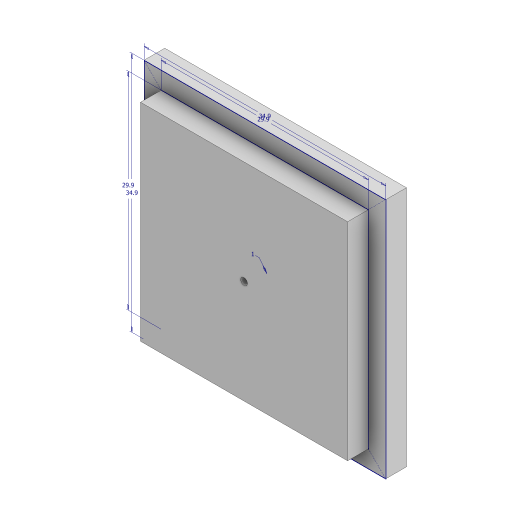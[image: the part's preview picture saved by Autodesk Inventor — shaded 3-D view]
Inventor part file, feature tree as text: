
AUTODESK INVENTOR PART (.ipt)
format: ipt  version: 2023 (Build 270158000, 158)  size: 114,688 bytes
history: native  units: in
note: dims shown in document units (in); Inventor stores cm internally (conversion verified against a paired STEP export)
features: extrude x2, sketch x1
ambient origin geometry x8: Origin, YZ Plane, XZ Plane, XY Plane, X Axis, Y Axis, Z Axis, Center Point
bodies: Solid1 (feature_tree)
feature tree (3):
  sketch  "Sketch1"  dims[d2=1.1772in d3=1.1772in d4=0.0394in d5=1.374in d6=1.374in d7=0.1181in d8=0.0in d9=0.1181in d10=0.0in]
  extrude  "Extrusion1"  Depth=1.1772in
  extrude  "Extrusion2"  Depth=0.1181in
